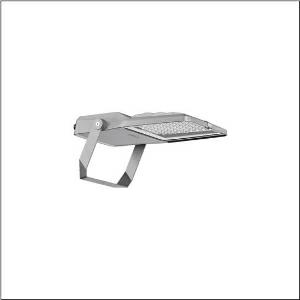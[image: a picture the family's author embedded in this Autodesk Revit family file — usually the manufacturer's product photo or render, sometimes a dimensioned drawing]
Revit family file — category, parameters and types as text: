
# Revit family: floodlight_fl_21_iq_mini___rs12_5xa7772c5b1a_b916
name_source: partatom
category: Lighting Fixtures
units: mm (PartAtom-declared; Revit-internal decimal feet)

## family parameters
Cut with Voids When Loaded = No
Host = Face
Light Source = No
Part Type = Normal
Room Calculation Point = No
Round Connector Dimension = Use Diameter
Shared = No

## types (1)
- --- (1 x LED, 11510 lm, 87.2 W, 4000K)
    Apparent Load = 87 VA
    CIE Flux Codes = 79 92 99 100 100
    Color Rendering = 80
    Color Temperature = 4000K
    Default Elevation = 1800 mm
    Description = Floodlight FL 21 iQ mini, floodlight, primary light control with lens, of PMMA, primary optical cover: protective disc, of toughened safety glass, transparent, light distribution: RS12, light emission: direct distribution, installation type: surface-mounted, LED, High Power LED, rated luminous flux: 11.510lm, luminous efficacy: 132lm/W, light colour: 840, colour temperature: 4000K, control gear: iQ Street-Remote/DALI, control: Street-Remote, Auto-Match, Temp-Guard, Night-Set, Smart-Wire, Desk-Remote (wireless, voltage-free reading and setting of iQ features in the workshop via application-optimized NFC function/RFID function), optimised constant luminous flux control (CLO 2.0), with terminal, 6-pole, mains connection: 220..240V, AC, 50/60Hz, start of lifetime: 87W, end of service life: 92W, reduction: 40W, luminaire housing, of diecast aluminium, powder-coated, Siteco® metallic grey (DB 702S), corrosivity category C5 mid according to DIN EN ISO 12944, suitable for swimming pools, chlorine-resistant, sealing non-destructively replaceable, mounting bracket, of steel, galvanised, powder-coated, Siteco® metallic grey (DB 702S), protection rating (complete): IP66, insulation class (complete): insulation class II (safety insulation), certification: CE, ENEC, VDE, protection symbol: D, impact resistance: IK08, permissible operating ambient temperature: -40..+40°C, permissible operating ambient temperature for outdoor applications: -40..+50°C, standard: DIN EN 12944, LABS conformity tested according to VDMA 24364:2018-05, packaging unit: 1 piece

Light Distribution: RS12
    Height = 70 mm
    Lamp = 1 x LED
    Lamp Light Flux = 11510 lm
    Lamp Power = 87.2 W
    Lamp count = 1
    Length = 485 mm
    Luminous efficacy = 132 lm/W
    Manufacturer = Siteco
    ModVariant = No
    Model = 5XA7772C5B1A
    Number of Poles = 1
    OnlyDefault = Yes
    Power Factor = 1
    Product Name = Floodlight FL 21 iQ mini | RS12
    Product group = floodlight | pylon annexe
    ProductGroupID = 6200
    Protection Class = Protection class II
    Protection Degree = IP 66
    RLX_Detail_Level = 1
    RLX_Emergency_Light_Flux = 0 lm
    RLX_Emergency_Type = 0
    RLX_Emergency_Type_DB = No
    RlxData = <blob elided: 90933 chars, md5=54b68b16>
    Socket = socket
    Standby Power = 0 W
    System Light Flux = 11510 lm
    System Power = 87 W
    Type Comments = factory setting: luminous flux: 100 % | dim-lin: 254 | 456 mA
    Type Image = l_1006845.jpg
    URL = http://relux.com
    VarID = @adj_167528
    Voltage = 0 V
    Weight = 0.00 kg
    Width = 337 mm

## geometry (parser evidence)
native form markers: Blend x4, Sweep x13
no freeform markers — native parametric forms only
